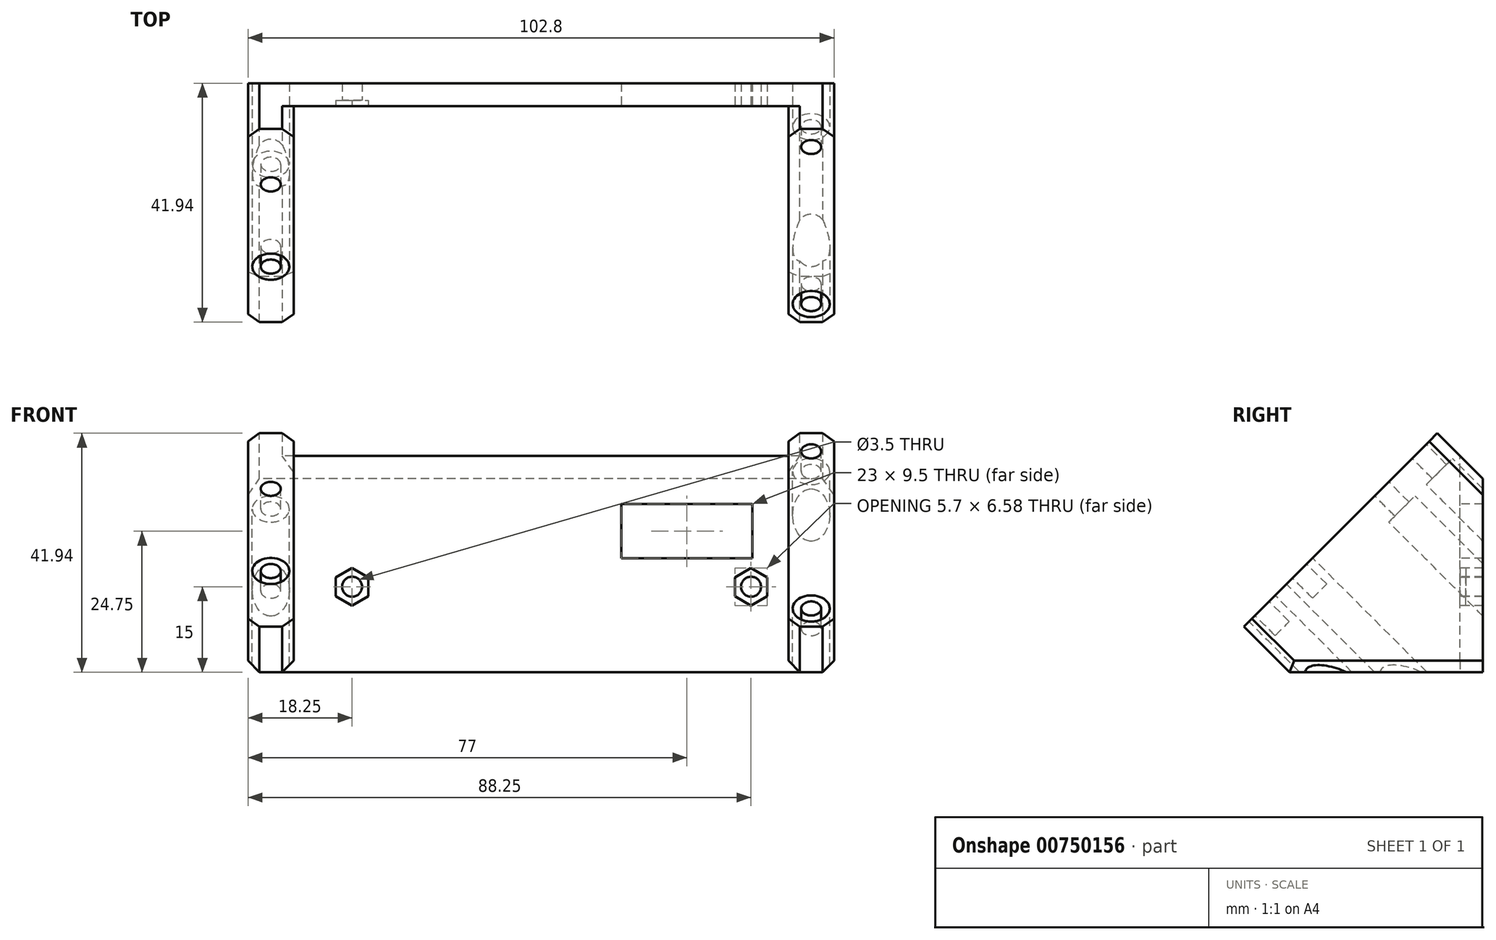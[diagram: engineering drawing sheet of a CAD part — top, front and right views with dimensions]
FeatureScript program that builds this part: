
annotation { "Feature Type Name" : "Feature", "Feature Type Description" : "" }
export const myFeature = defineFeature(function(context is Context, id is Id, definition is map)
    precondition{}
    {
        {
            var Q0;
            Q0=qCreatedBy(makeId("Right.planeOp"),FACE);
            var sketch = newSketch(context, id + "F0", { "sketchPlane" : qUnion([Q0])});
            skLineSegment(sketch, "E0", {"start": v(0, 0) * mm, "end": v(-38.3, 38.3) * mm, "construction": true});
            skLineSegment(sketch, "E1", {"start": v(-24.97, 24.97) * mm, "end": v(-38.3, 38.3) * mm});
            skLineSegment(sketch, "E2", {"start": v(-24.97, 24.97) * mm, "end": v(-8, 41.94) * mm});
            skLineSegment(sketch, "E3", {"start": v(-8, 41.94) * mm, "end": v(0, 33.94) * mm});
            skLineSegment(sketch, "E4.MirrorCS", {"start": v(-24.97, 24.97) * mm, "end": v(-41.94, 8) * mm});
            skLineSegment(sketch, "E5.MirrorCS", {"start": v(-41.94, 8) * mm, "end": v(-33.94, 0) * mm});
            skLineSegment(sketch, "E6", {"start": v(-33.94, 0) * mm, "end": v(0, 0) * mm});
            skLineSegment(sketch, "E7", {"start": v(0, 33.94) * mm, "end": v(0, 0) * mm});
            skLineSegment(sketch, "E8", {"start": v(-4, 0) * mm, "end": v(-4, 37.94) * mm});
            skSolve(sketch);
        }
        {
            var Q0;
            Q0=sQuery(id+"F0.wireOp",VERTEX,"E1.start");
            var Q1;
            Q1=sQuery(id+"F0.wireOp",EDGE,"E1");
            cPlane(context, id + "F1", {"entities" : qUnion([Q0, Q1]), "cplaneType" : CPlaneType.LINE_POINT, "offset" : 25 * mm, "width" : 150 * mm, "height" : 150 * mm});
        }
        {
            var Q0;
            {var subQ2=sQuery(id+"F0.wireOp",EDGE,"E2");Q0=makeQuery(id+"F0.imprint","IMPRINT",FACE,{"disambiguationData":[TD([[makeQuery(id+"F0.imprint","IMPRINT",EDGE,{"derivedFrom":subQ2}),-1.0]])]});}
            extrude(context, id + "F2", {"entities" : qUnion([Q0]), "depth" : 8 * mm, "offsetDistance" : 25 * mm, "symmetric" : true});
        }
        {
            var Q0;
            Q0=makeQuery(id+"F2.opExtrude","SWEPT_BODY",BODY,{"disambiguationData":[OSD([sQuery(id+"F0.wireOp",EDGE,"E2"),sQuery(id+"F0.wireOp",EDGE,"E3"),sQuery(id+"F0.wireOp",EDGE,"E4.MirrorCS"),sQuery(id+"F0.wireOp",EDGE,"E5.MirrorCS"),sQuery(id+"F0.wireOp",EDGE,"E6"),sQuery(id+"F0.wireOp",EDGE,"E8")])]});
            var Q1;
            Q1=makeQuery(id+"F2.opExtrude","SWEPT_EDGE",EDGE,{"disambiguationData":[OSD([sQuery(id+"F0.wireOp",EDGE,"E2"),sQuery(id+"F0.wireOp",EDGE,"E3")])]});
            transform(context, id + "F3", {"entities" : qUnion([Q0]), "transformType" : TransformType.TRANSLATION_DISTANCE, "transformDirection" : qUnion([Q1]), "distance" : 49.25 * mm, "makeCopy" : true});
        }
        {
            var Q0;
            Q0=makeQuery(id+"F2.opExtrude","SWEPT_BODY",BODY,{"disambiguationData":[OSD([sQuery(id+"F0.wireOp",EDGE,"E2"),sQuery(id+"F0.wireOp",EDGE,"E3"),sQuery(id+"F0.wireOp",EDGE,"E4.MirrorCS"),sQuery(id+"F0.wireOp",EDGE,"E5.MirrorCS"),sQuery(id+"F0.wireOp",EDGE,"E6"),sQuery(id+"F0.wireOp",EDGE,"E8")])]});
            var Q1;
            Q1=makeQuery(id+"F2.opExtrude","SWEPT_EDGE",EDGE,{"disambiguationData":[OSD([sQuery(id+"F0.wireOp",EDGE,"E2"),sQuery(id+"F0.wireOp",EDGE,"E3")])]});
            transform(context, id + "F4", {"entities" : qUnion([Q0]), "transformType" : TransformType.TRANSLATION_DISTANCE, "transformDirection" : qUnion([Q1]), "distance" : 45.55 * mm, "oppositeDirection" : true, "makeCopy" : false});
        }
        {
            var Q0;
            {var subQ0=sQuery(id+"F0.wireOp",EDGE,"E7");Q0=makeQuery(id+"F0.imprint","IMPRINT",FACE,{"disambiguationData":[TD([[makeQuery(id+"F0.imprint","IMPRINT",EDGE,{"derivedFrom":subQ0}),-1.0]])]});}
            var Q1;
            Q1=makeQuery(id+"F2.opExtrude","CAP_FACE",FACE,{"disambiguationData":[OSD([sQuery(id+"F0.wireOp",EDGE,"E2"),sQuery(id+"F0.wireOp",EDGE,"E3"),sQuery(id+"F0.wireOp",EDGE,"E4.MirrorCS"),sQuery(id+"F0.wireOp",EDGE,"E5.MirrorCS"),sQuery(id+"F0.wireOp",EDGE,"E6"),sQuery(id+"F0.wireOp",EDGE,"E8")])],"isStart":false});
            var Q2;
            Q2=makeQuery(id+"F3.opPattern","COPY",FACE,{"derivedFrom":makeQuery(id+"F2.opExtrude","CAP_FACE",FACE,{"disambiguationData":[OSD([sQuery(id+"F0.wireOp",EDGE,"E2"),sQuery(id+"F0.wireOp",EDGE,"E3"),sQuery(id+"F0.wireOp",EDGE,"E4.MirrorCS"),sQuery(id+"F0.wireOp",EDGE,"E5.MirrorCS"),sQuery(id+"F0.wireOp",EDGE,"E6"),sQuery(id+"F0.wireOp",EDGE,"E8")])],"isStart":true}),"instanceName":"1"});
            extrude(context, id + "F5", {"entities" : qUnion([Q0]), "operationType" : NewBodyOperationType.ADD, "endBound" : BoundingType.UP_TO_SURFACE, "depth" : 25 * mm, "endBoundEntityFace" : qUnion([Q1]), "offsetDistance" : 25 * mm, "hasSecondDirection" : true, "secondDirectionBound" : BoundingType.UP_TO_SURFACE, "secondDirectionOppositeDirection" : true, "secondDirectionDepth" : 25 * mm, "secondDirectionBoundEntityFace" : qUnion([Q2])});
        }
        {
            var Q0;
            Q0=qCreatedBy(id+"F1.planeOp",FACE);
            var sketch = newSketch(context, id + "F6", { "sketchPlane" : qUnion([Q0])});
            skCircle(sketch, "E9", {"center": v(-49.25, 10.2) * mm, "radius": 1.75 * mm});
            skPoint(sketch, "E10", {"position": v(-49.25, 24) * mm});
            skPoint(sketch, "E11", {"position": v(45.55, 24) * mm});
            skCircle(sketch, "E12", {"center": v(45.55, 19.5) * mm, "radius": 1.75 * mm});
            skLineSegment(sketch, "E13", {"start": v(-53.25, 0) * mm, "end": v(-55.34, 0) * mm, "construction": true});
            skCircle(sketch, "E14.MirrorC", {"center": v(-49.25, -10.2) * mm, "radius": 1.75 * mm});
            skCircle(sketch, "E15.MirrorC", {"center": v(45.55, -19.5) * mm, "radius": 1.75 * mm});
            skCircle(sketch, "E16", {"center": v(-49.25, 10.2) * mm, "radius": 3.25 * mm});
            skCircle(sketch, "E17.MirrorC", {"center": v(-49.25, -10.2) * mm, "radius": 3.25 * mm});
            skCircle(sketch, "E18", {"center": v(45.55, 19.5) * mm, "radius": 3.25 * mm});
            skCircle(sketch, "E19.MirrorC", {"center": v(45.55, -19.5) * mm, "radius": 3.25 * mm});
            skLineSegment(sketch, "E20", {"start": v(53.25, 17.25) * mm, "end": v(53.25, -24) * mm, "construction": true});
            skLineSegment(sketch, "E21.bottom", {"start": v(34.25, 5) * mm, "end": v(13.25, 5) * mm, "construction": true});
            skLineSegment(sketch, "E21.top", {"start": v(34.25, 12.5) * mm, "end": v(13.25, 12.5) * mm, "construction": true});
            skLineSegment(sketch, "E21.left", {"start": v(34.25, 5) * mm, "end": v(34.25, 12.5) * mm, "construction": true});
            skLineSegment(sketch, "E21.right", {"start": v(13.25, 5) * mm, "end": v(13.25, 12.5) * mm, "construction": true});
            skSolve(sketch);
        }
        {
            var Q0;
            Q0=makeQuery(id+"F6.imprint","IMPRINT",FACE,{"disambiguationData":[TD([[makeQuery(id+"F6.imprint","IMPRINT",EDGE,{"derivedFrom":sQuery(id+"F6.wireOp",EDGE,"E9")}),-1.0]])]});
            var Q1;
            Q1=makeQuery(id+"F6.imprint","IMPRINT",FACE,{"disambiguationData":[TD([[makeQuery(id+"F6.imprint","IMPRINT",EDGE,{"derivedFrom":sQuery(id+"F6.wireOp",EDGE,"E9")}),1.0]])]});
            var Q2;
            Q2=makeQuery(id+"F6.imprint","IMPRINT",FACE,{"disambiguationData":[TD([[makeQuery(id+"F6.imprint","IMPRINT",EDGE,{"derivedFrom":sQuery(id+"F6.wireOp",EDGE,"E14.MirrorC")}),1.0]])]});
            var Q3;
            Q3=makeQuery(id+"F6.imprint","IMPRINT",FACE,{"disambiguationData":[TD([[makeQuery(id+"F6.imprint","IMPRINT",EDGE,{"derivedFrom":sQuery(id+"F6.wireOp",EDGE,"E14.MirrorC")}),-1.0]])]});
            var Q4;
            Q4=makeQuery(id+"F6.imprint","IMPRINT",FACE,{"disambiguationData":[TD([[makeQuery(id+"F6.imprint","IMPRINT",EDGE,{"derivedFrom":sQuery(id+"F6.wireOp",EDGE,"E12")}),-1.0]])]});
            var Q5;
            Q5=makeQuery(id+"F6.imprint","IMPRINT",FACE,{"disambiguationData":[TD([[makeQuery(id+"F6.imprint","IMPRINT",EDGE,{"derivedFrom":sQuery(id+"F6.wireOp",EDGE,"E12")}),1.0]])]});
            var Q6;
            Q6=makeQuery(id+"F6.imprint","IMPRINT",FACE,{"disambiguationData":[TD([[makeQuery(id+"F6.imprint","IMPRINT",EDGE,{"derivedFrom":sQuery(id+"F6.wireOp",EDGE,"E15.MirrorC")}),1.0]])]});
            var Q7;
            Q7=makeQuery(id+"F6.imprint","IMPRINT",FACE,{"disambiguationData":[TD([[makeQuery(id+"F6.imprint","IMPRINT",EDGE,{"derivedFrom":sQuery(id+"F6.wireOp",EDGE,"E15.MirrorC")}),-1.0]])]});
            extrude(context, id + "F7", {"entities" : qUnion([Q0, Q1, Q2, Q3, Q4, Q5, Q6, Q7]), "operationType" : NewBodyOperationType.REMOVE, "endBound" : BoundingType.THROUGH_ALL, "oppositeDirection" : true, "depth" : 25 * mm, "offsetDistance" : 25 * mm});
        }
        {
            var Q0;
            Q0=makeQuery(id+"F6.imprint","IMPRINT",FACE,{"disambiguationData":[TD([[makeQuery(id+"F6.imprint","IMPRINT",EDGE,{"derivedFrom":sQuery(id+"F6.wireOp",EDGE,"E15.MirrorC")}),1.0]])]});
            var Q1;
            Q1=makeQuery(id+"F6.imprint","IMPRINT",FACE,{"disambiguationData":[TD([[makeQuery(id+"F6.imprint","IMPRINT",EDGE,{"derivedFrom":sQuery(id+"F6.wireOp",EDGE,"E12")}),-1.0]])]});
            var Q2;
            Q2=makeQuery(id+"F6.imprint","IMPRINT",FACE,{"disambiguationData":[TD([[makeQuery(id+"F6.imprint","IMPRINT",EDGE,{"derivedFrom":sQuery(id+"F6.wireOp",EDGE,"E9")}),-1.0]])]});
            var Q3;
            Q3=makeQuery(id+"F6.imprint","IMPRINT",FACE,{"disambiguationData":[TD([[makeQuery(id+"F6.imprint","IMPRINT",EDGE,{"derivedFrom":sQuery(id+"F6.wireOp",EDGE,"E14.MirrorC")}),1.0]])]});
            extrude(context, id + "F8", {"entities" : qUnion([Q0, Q1, Q2, Q3]), "operationType" : NewBodyOperationType.ADD, "oppositeDirection" : true, "depth" : 5 * mm, "offsetDistance" : 25 * mm});
        }
        {
            var Q0;
            Q0=makeQuery(id+"F5.opExtrude","SWEPT_FACE",FACE,{"disambiguationData":[OSD([sQuery(id+"F0.wireOp",EDGE,"E8")])]});
            var sketch = newSketch(context, id + "F9", { "sketchPlane" : qUnion([Q0])});
            skLineSegment(sketch, "E22.bottom", {"start": v(12.25, 20) * mm, "end": v(35.25, 20) * mm});
            skLineSegment(sketch, "E22.top", {"start": v(12.25, 29.5) * mm, "end": v(35.25, 29.5) * mm});
            skLineSegment(sketch, "E22.left", {"start": v(12.25, 20) * mm, "end": v(12.25, 29.5) * mm});
            skLineSegment(sketch, "E22.right", {"start": v(35.25, 20) * mm, "end": v(35.25, 29.5) * mm});
            skPoint(sketch, "E23", {"position": v(23.75, 20) * mm});
            skCircle(sketch, "E24", {"center": v(-35, 15) * mm, "radius": 1.75 * mm});
            skCircle(sketch, "E25.cCircle", {"center": v(-35, 15) * mm, "radius": 2.85 * mm, "construction": true});
            skLineSegment(sketch, "E25.0", {"start": v(-32.15, 16.65) * mm, "end": v(-32.15, 13.35) * mm});
            skLineSegment(sketch, "E25.1", {"start": v(-32.15, 13.35) * mm, "end": v(-35, 11.7) * mm});
            skLineSegment(sketch, "E25.2", {"start": v(-35, 11.7) * mm, "end": v(-37.85, 13.35) * mm});
            skLineSegment(sketch, "E25.3", {"start": v(-37.85, 13.35) * mm, "end": v(-37.85, 16.65) * mm});
            skLineSegment(sketch, "E25.4", {"start": v(-37.85, 16.65) * mm, "end": v(-35, 18.3) * mm});
            skLineSegment(sketch, "E25.5", {"start": v(-35, 18.3) * mm, "end": v(-32.15, 16.65) * mm});
            skPoint(sketch, "E25.0.midPoint", {"position": v(-32.15, 15) * mm});
            skLineSegment(sketch, "E26.MirrorCS", {"start": v(37.85, 16.65) * mm, "end": v(35, 18.3) * mm});
            skLineSegment(sketch, "E27.MirrorCS", {"start": v(35, 18.3) * mm, "end": v(32.15, 16.65) * mm});
            skLineSegment(sketch, "E28.MirrorCS", {"start": v(35, 11.7) * mm, "end": v(37.85, 13.35) * mm});
            skLineSegment(sketch, "E29.MirrorCS", {"start": v(32.15, 13.35) * mm, "end": v(35, 11.7) * mm});
            skLineSegment(sketch, "E30.MirrorCS", {"start": v(37.85, 13.35) * mm, "end": v(37.85, 16.65) * mm});
            skLineSegment(sketch, "E31.MirrorCS", {"start": v(32.15, 16.65) * mm, "end": v(32.15, 13.35) * mm});
            skCircle(sketch, "E32.MirrorC", {"center": v(35, 15) * mm, "radius": 2.85 * mm, "construction": true});
            skPoint(sketch, "E33.MirrorP", {"position": v(32.15, 15) * mm});
            skCircle(sketch, "E34.MirrorC", {"center": v(35, 15) * mm, "radius": 1.75 * mm});
            skSolve(sketch);
        }
        {
            var Q0;
            Q0=makeQuery(id+"F9.imprint","IMPRINT",FACE,{"disambiguationData":[TD([[makeQuery(id+"F9.imprint","IMPRINT",EDGE,{"derivedFrom":sQuery(id+"F9.wireOp",EDGE,"E24")}),1.0]])]});
            var Q1;
            Q1=makeQuery(id+"F9.imprint","IMPRINT",FACE,{"disambiguationData":[TD([[makeQuery(id+"F9.imprint","IMPRINT",EDGE,{"derivedFrom":sQuery(id+"F9.wireOp",EDGE,"E34.MirrorC")}),-1.0]])]});
            var Q2;
            Q2=makeQuery(id+"F9.imprint","IMPRINT",FACE,{"disambiguationData":[TD([[makeQuery(id+"F9.imprint","IMPRINT",EDGE,{"derivedFrom":sQuery(id+"F9.wireOp",EDGE,"E22.bottom")}),1.0]])]});
            extrude(context, id + "F10", {"entities" : qUnion([Q0, Q1, Q2]), "operationType" : NewBodyOperationType.REMOVE, "endBound" : BoundingType.THROUGH_ALL, "oppositeDirection" : true, "depth" : 25 * mm, "offsetDistance" : 25 * mm});
        }
        {
            var Q0;
            Q0=makeQuery(id+"F9.imprint","IMPRINT",FACE,{"disambiguationData":[TD([[makeQuery(id+"F9.imprint","IMPRINT",EDGE,{"derivedFrom":sQuery(id+"F9.wireOp",EDGE,"E24")}),-1.0]])]});
            var Q1;
            Q1=makeQuery(id+"F9.imprint","IMPRINT",FACE,{"disambiguationData":[TD([[makeQuery(id+"F9.imprint","IMPRINT",EDGE,{"derivedFrom":sQuery(id+"F9.wireOp",EDGE,"E26.MirrorCS")}),1.0]])]});
            extrude(context, id + "F11", {"entities" : qUnion([Q0, Q1]), "operationType" : NewBodyOperationType.REMOVE, "oppositeDirection" : true, "depth" : 1 * mm, "offsetDistance" : 25 * mm});
        }
        {
            var Q0;
            {var subQ0=sQuery(id+"F0.wireOp",EDGE,"E3");Q0=makeQuery(id+"F5.boolean.opBoolean","MERGE",EDGE,{"derivedFrom":[makeQuery(id+"F2.opExtrude","CAP_EDGE",EDGE,{"disambiguationData":[OSD([subQ0])],"isStart":false}),makeQuery(id+"F5.opExtrude","CAP_EDGE",EDGE,{"disambiguationData":[OSD([subQ0])],"isStart":false})]});}
            var Q1;
            Q1=makeQuery(id+"F2.opExtrude","CAP_EDGE",EDGE,{"disambiguationData":[OSD([sQuery(id+"F0.wireOp",EDGE,"E3")])],"isStart":true});
            var Q2;
            {var subQ0=sQuery(id+"F0.wireOp",EDGE,"E3");Q2=makeQuery(id+"F5.boolean.opBoolean","MERGE",EDGE,{"derivedFrom":[makeQuery(id+"F3.opPattern","COPY",EDGE,{"derivedFrom":makeQuery(id+"F2.opExtrude","CAP_EDGE",EDGE,{"disambiguationData":[OSD([subQ0])],"isStart":true}),"instanceName":"1"}),makeQuery(id+"F5.opExtrude","CAP_EDGE",EDGE,{"disambiguationData":[OSD([subQ0])],"isStart":true})]});}
            var Q3;
            Q3=makeQuery(id+"F3.opPattern","COPY",EDGE,{"derivedFrom":makeQuery(id+"F2.opExtrude","CAP_EDGE",EDGE,{"disambiguationData":[OSD([sQuery(id+"F0.wireOp",EDGE,"E3")])],"isStart":false}),"instanceName":"1"});
            var Q4;
            {var subQ0=sQuery(id+"F0.wireOp",EDGE,"E6");Q4=makeQuery(id+"F5.boolean.opBoolean","MERGE",EDGE,{"derivedFrom":[makeQuery(id+"F3.opPattern","COPY",EDGE,{"derivedFrom":makeQuery(id+"F2.opExtrude","CAP_EDGE",EDGE,{"disambiguationData":[OSD([subQ0])],"isStart":true}),"instanceName":"1"}),makeQuery(id+"F5.opExtrude","CAP_EDGE",EDGE,{"disambiguationData":[OSD([subQ0])],"isStart":true})]});}
            var Q5;
            Q5=makeQuery(id+"F3.opPattern","COPY",EDGE,{"derivedFrom":makeQuery(id+"F2.opExtrude","CAP_EDGE",EDGE,{"disambiguationData":[OSD([sQuery(id+"F0.wireOp",EDGE,"E6")])],"isStart":false}),"instanceName":"1"});
            var Q6;
            Q6=makeQuery(id+"F3.opPattern","COPY",EDGE,{"derivedFrom":makeQuery(id+"F2.opExtrude","CAP_EDGE",EDGE,{"disambiguationData":[OSD([sQuery(id+"F0.wireOp",EDGE,"E5.MirrorCS")])],"isStart":true}),"instanceName":"1"});
            var Q7;
            Q7=makeQuery(id+"F3.opPattern","COPY",EDGE,{"derivedFrom":makeQuery(id+"F2.opExtrude","CAP_EDGE",EDGE,{"disambiguationData":[OSD([sQuery(id+"F0.wireOp",EDGE,"E5.MirrorCS")])],"isStart":false}),"instanceName":"1"});
            var Q8;
            Q8=makeQuery(id+"F2.opExtrude","CAP_EDGE",EDGE,{"disambiguationData":[OSD([sQuery(id+"F0.wireOp",EDGE,"E5.MirrorCS")])],"isStart":true});
            var Q9;
            Q9=makeQuery(id+"F2.opExtrude","CAP_EDGE",EDGE,{"disambiguationData":[OSD([sQuery(id+"F0.wireOp",EDGE,"E5.MirrorCS")])],"isStart":false});
            var Q10;
            Q10=makeQuery(id+"F2.opExtrude","CAP_EDGE",EDGE,{"disambiguationData":[OSD([sQuery(id+"F0.wireOp",EDGE,"E6")])],"isStart":true});
            var Q11;
            {var subQ0=sQuery(id+"F0.wireOp",EDGE,"E6");Q11=makeQuery(id+"F5.boolean.opBoolean","MERGE",EDGE,{"derivedFrom":[makeQuery(id+"F2.opExtrude","CAP_EDGE",EDGE,{"disambiguationData":[OSD([subQ0])],"isStart":false}),makeQuery(id+"F5.opExtrude","CAP_EDGE",EDGE,{"disambiguationData":[OSD([subQ0])],"isStart":false})]});}
            var Q12;
            {var subQ0=sQuery(id+"F0.wireOp",EDGE,"E8");var subQ1=sQuery(id+"F0.wireOp",EDGE,"E3");Q12=makeQuery(id+"F5.opExtrude","TWEAK_EDGE",EDGE,{"derivedFrom":[makeQuery(id+"F0.imprint","IMPRINT",EDGE,{"disambiguationData":[TD([[makeQuery(id+"F0.imprint","INTERSECT",VERTEX,{"derivedFrom":[subQ1,sQuery(id+"F0.wireOp",EDGE,"E7")]}),1.0]])],"derivedFrom":subQ1}),makeQuery(id+"F0.imprint","IMPRINT",EDGE,{"derivedFrom":subQ0})]});}
            chamfer(context, id + "F12", {"entities" : qUnion([Q0, Q1, Q2, Q3, Q4, Q5, Q6, Q7, Q8, Q9, Q10, Q11, Q12]), "width" : 2 * mm, "tangentPropagation" : true});
        }
    });
